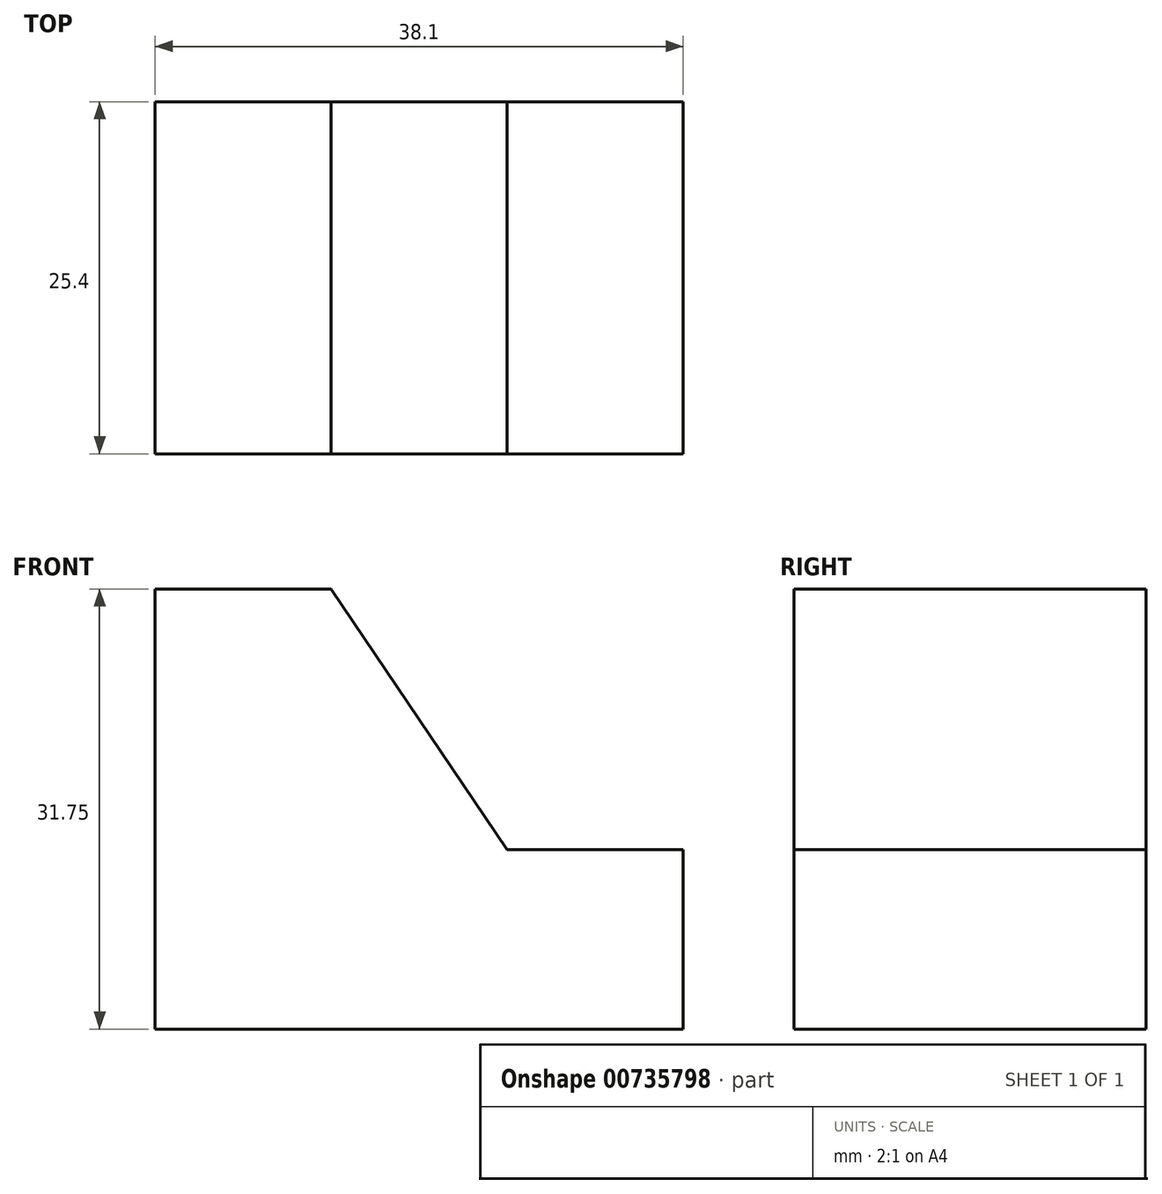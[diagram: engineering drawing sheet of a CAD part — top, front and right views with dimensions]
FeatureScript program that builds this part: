
annotation { "Feature Type Name" : "Feature", "Feature Type Description" : "" }
export const myFeature = defineFeature(function(context is Context, id is Id, definition is map)
    precondition{}
    {
        {
            var Q0;
            Q0=qCreatedBy(makeId("Front.planeOp"),FACE);
            var sketch = newSketch(context, id + "F0", { "sketchPlane" : qUnion([Q0])});
            skLineSegment(sketch, "E0", {"start": v(0, 0) * mm, "end": v(38.1, 0) * mm});
            skLineSegment(sketch, "E1", {"start": v(38.1, 0) * mm, "end": v(38.1, 31.75) * mm});
            skLineSegment(sketch, "E2", {"start": v(38.1, 31.75) * mm, "end": v(0, 31.75) * mm});
            skLineSegment(sketch, "E3", {"start": v(0, 31.75) * mm, "end": v(0, 0) * mm});
            skSolve(sketch);
        }
        {
            var Q0;
            Q0=makeQuery(id+"F0.imprint","IMPRINT",FACE,{"disambiguationData":[TD([[makeQuery(id+"F0.imprint","IMPRINT",EDGE,{"derivedFrom":sQuery(id+"F0.wireOp",EDGE,"E0")}),1.0]])]});
            extrude(context, id + "F1", {"entities" : qUnion([Q0]), "oppositeDirection" : true, "depth" : 25.4 * mm, "offsetDistance" : 25.4 * mm});
        }
        {
            var Q0;
            Q0=makeQuery(id+"F1.opExtrude","CAP_FACE",FACE,{"disambiguationData":[OSD([sQuery(id+"F0.wireOp",EDGE,"E0"),sQuery(id+"F0.wireOp",EDGE,"E1"),sQuery(id+"F0.wireOp",EDGE,"E2"),sQuery(id+"F0.wireOp",EDGE,"E3")])],"isStart":true});
            var sketch = newSketch(context, id + "F2", { "sketchPlane" : qUnion([Q0])});
            skLineSegment(sketch, "E4", {"start": v(38.1, 12.93) * mm, "end": v(25.4, 12.93) * mm});
            skLineSegment(sketch, "E5", {"start": v(25.4, 12.93) * mm, "end": v(12.7, 31.75) * mm});
            skLineSegment(sketch, "E6", {"start": v(12.7, 31.75) * mm, "end": v(38.1, 31.75) * mm});
            skLineSegment(sketch, "E7", {"start": v(38.1, 31.75) * mm, "end": v(38.1, 12.93) * mm});
            skSolve(sketch);
        }
        {
            var Q0;
            Q0=makeQuery(id+"F2.imprint","IMPRINT",FACE,{"disambiguationData":[TD([[makeQuery(id+"F2.imprint","IMPRINT",EDGE,{"derivedFrom":sQuery(id+"F2.wireOp",EDGE,"E4")}),-1.0]])]});
            extrude(context, id + "F3", {"entities" : qUnion([Q0]), "operationType" : NewBodyOperationType.REMOVE, "oppositeDirection" : true, "depth" : 25.4 * mm, "offsetDistance" : 25.4 * mm});
        }
    });
